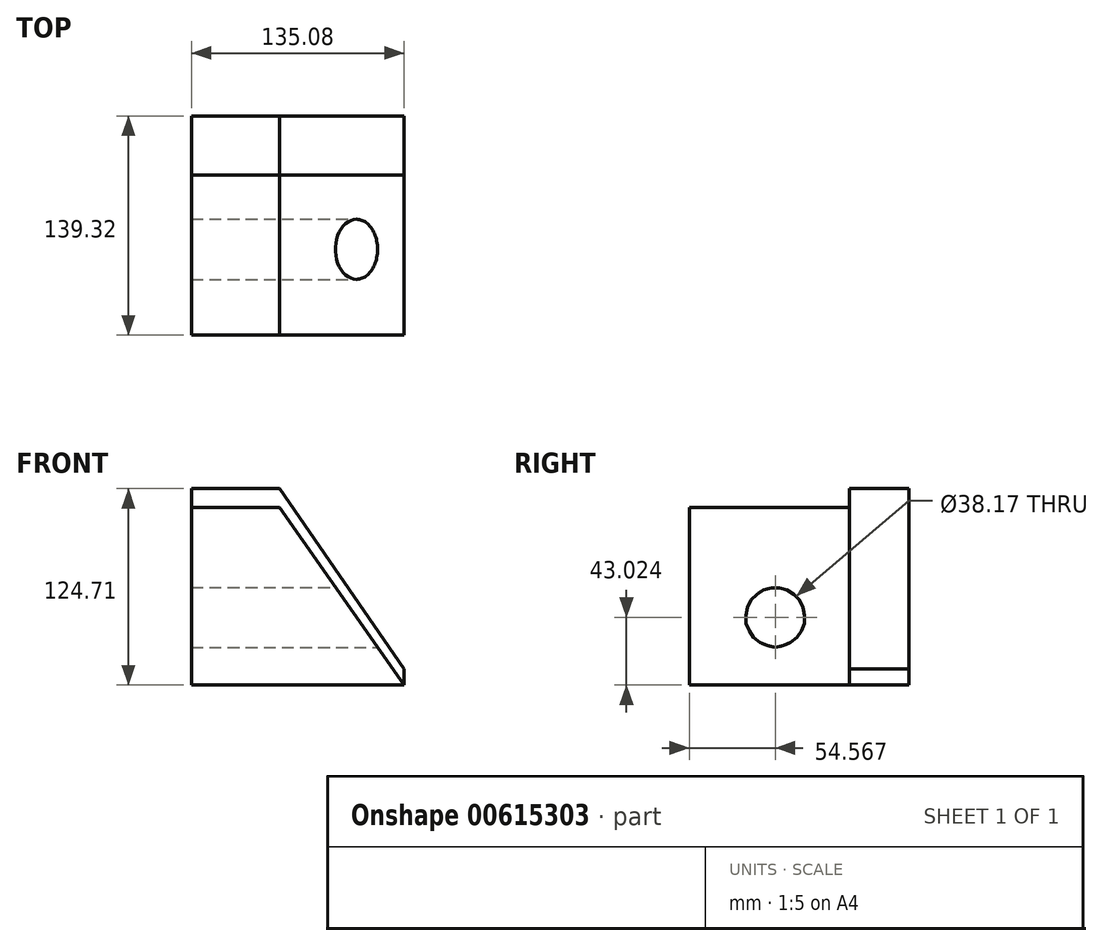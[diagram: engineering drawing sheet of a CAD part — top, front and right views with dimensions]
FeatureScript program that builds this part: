
annotation { "Feature Type Name" : "Feature", "Feature Type Description" : "" }
export const myFeature = defineFeature(function(context is Context, id is Id, definition is map)
    precondition{}
    {
        {
            var Q0;
            Q0=qCreatedBy(makeId("Top.planeOp"),FACE);
            var sketch = newSketch(context, id + "F0", { "sketchPlane" : qUnion([Q0])});
            skLineSegment(sketch, "E0.bottom", {"start": v(-67.54, 69.66) * mm, "end": v(67.54, 69.66) * mm});
            skLineSegment(sketch, "E0.top", {"start": v(-67.54, -69.66) * mm, "end": v(67.54, -69.66) * mm});
            skLineSegment(sketch, "E0.left", {"start": v(-67.54, 69.66) * mm, "end": v(-67.54, -69.66) * mm});
            skLineSegment(sketch, "E0.right", {"start": v(67.54, 69.66) * mm, "end": v(67.54, -69.66) * mm});
            skPoint(sketch, "E0.middle", {"position": v(0, 0) * mm});
            skSolve(sketch);
        }
        {
            var Q0;
            Q0=makeQuery(id+"F0.imprint","IMPRINT",FACE,{"disambiguationData":[TD([[makeQuery(id+"F0.imprint","IMPRINT",EDGE,{"derivedFrom":sQuery(id+"F0.wireOp",EDGE,"E0.bottom")}),-1.0]])]});
            extrude(context, id + "F1", {"entities" : qUnion([Q0]), "depth" : 124.7 * mm, "offsetDistance" : 25.4 * mm});
        }
        {
            var Q0;
            Q0=makeQuery(id+"F1.opExtrude","SWEPT_FACE",FACE,{"disambiguationData":[OSD([sQuery(id+"F0.wireOp",EDGE,"E0.top")])]});
            var sketch = newSketch(context, id + "F2", { "sketchPlane" : qUnion([Q0])});
            skLineSegment(sketch, "E1", {"start": v(-20.1, 124.71) * mm, "end": v(67.54, 124.71) * mm});
            skLineSegment(sketch, "E2", {"start": v(67.54, 124.71) * mm, "end": v(67.54, 0) * mm});
            skLineSegment(sketch, "E3", {"start": v(67.54, 0) * mm, "end": v(-20.1, 124.71) * mm});
            skSolve(sketch);
        }
        {
            var Q0;
            Q0=makeQuery(id+"F2.imprint","IMPRINT",FACE,{"disambiguationData":[TD([[makeQuery(id+"F2.imprint","IMPRINT",EDGE,{"derivedFrom":sQuery(id+"F2.wireOp",EDGE,"E1")}),-1.0]])]});
            extrude(context, id + "F3", {"entities" : qUnion([Q0]), "operationType" : NewBodyOperationType.REMOVE, "endBound" : BoundingType.SYMMETRIC, "depth" : 203.2 * mm, "offsetDistance" : 25.4 * mm});
        }
        {
            var Q0;
            Q0=makeQuery(id+"F1.opExtrude","SWEPT_FACE",FACE,{"disambiguationData":[OSD([sQuery(id+"F0.wireOp",EDGE,"E0.top")])]});
            var sketch = newSketch(context, id + "F4", { "sketchPlane" : qUnion([Q0])});
            skLineSegment(sketch, "E4", {"start": v(-11.7, 112.75) * mm, "end": v(-67.54, 112.75) * mm});
            skLineSegment(sketch, "E5", {"start": v(-67.54, 112.75) * mm, "end": v(-67.54, 124.71) * mm});
            skLineSegment(sketch, "E6", {"start": v(-67.54, 124.71) * mm, "end": v(-20.1, 124.71) * mm});
            skLineSegment(sketch, "E7", {"start": v(-20.1, 124.71) * mm, "end": v(-11.7, 112.75) * mm});
            skSolve(sketch);
        }
        {
            var Q0;
            Q0=makeQuery(id+"F4.imprint","IMPRINT",FACE,{"disambiguationData":[TD([[makeQuery(id+"F4.imprint","IMPRINT",EDGE,{"derivedFrom":sQuery(id+"F4.wireOp",EDGE,"E4")}),-1.0]])]});
            extrude(context, id + "F5", {"entities" : qUnion([Q0]), "operationType" : NewBodyOperationType.REMOVE, "oppositeDirection" : true, "depth" : 101.6 * mm, "offsetDistance" : 25.4 * mm});
        }
        {
            var Q0;
            Q0=makeQuery(id+"F5.boolean.opBoolean","MERGE",FACE,{"derivedFrom":[makeQuery(id+"F3.boolean.opBoolean","COPY",FACE,{"derivedFrom":makeQuery(id+"F3.opExtrude","CAP_FACE",FACE,{"disambiguationData":[OSD([sQuery(id+"F2.wireOp",EDGE,"E1"),sQuery(id+"F2.wireOp",EDGE,"E2"),sQuery(id+"F2.wireOp",EDGE,"E3")])],"isStart":true})}),makeQuery(id+"F5.opExtrude","CAP_FACE",FACE,{"disambiguationData":[OSD([sQuery(id+"F4.wireOp",EDGE,"E4"),sQuery(id+"F4.wireOp",EDGE,"E5"),sQuery(id+"F4.wireOp",EDGE,"E6"),sQuery(id+"F4.wireOp",EDGE,"E7")])],"isStart":false})]});
            var sketch = newSketch(context, id + "F6", { "sketchPlane" : qUnion([Q0])});
            skLineSegment(sketch, "E8", {"start": v(-11.7, 124.71) * mm, "end": v(67.54, 124.71) * mm});
            skLineSegment(sketch, "E9", {"start": v(67.54, 124.71) * mm, "end": v(67.54, 10.25) * mm});
            skLineSegment(sketch, "E10", {"start": v(67.54, 10.25) * mm, "end": v(-11.7, 124.71) * mm});
            skSolve(sketch);
        }
        {
            var Q0;
            Q0=makeQuery(id+"F6.imprint","IMPRINT",FACE,{"disambiguationData":[TD([[makeQuery(id+"F6.imprint","IMPRINT",EDGE,{"derivedFrom":sQuery(id+"F6.wireOp",EDGE,"E8")}),-1.0]])]});
            extrude(context, id + "F7", {"entities" : qUnion([Q0]), "operationType" : NewBodyOperationType.REMOVE, "oppositeDirection" : true, "depth" : 50.8 * mm, "offsetDistance" : 25.4 * mm});
        }
        {
            var Q0;
            Q0=qCreatedBy(makeId("Right.planeOp"),FACE);
            var sketch = newSketch(context, id + "F8", { "sketchPlane" : qUnion([Q0])});
            skCircle(sketch, "E11", {"center": v(-15.1, 43.02) * mm, "radius": 19.09 * mm});
            skSolve(sketch);
        }
        {
            var Q0;
            Q0 = qSketchRegion(id + "F8", true);
            extrude(context, id + "F9", {"entities" : qUnion([Q0]), "operationType" : NewBodyOperationType.REMOVE, "endBound" : BoundingType.SYMMETRIC, "oppositeDirection" : true, "depth" : 276.35 * mm, "offsetDistance" : 25.4 * mm});
        }
    });
